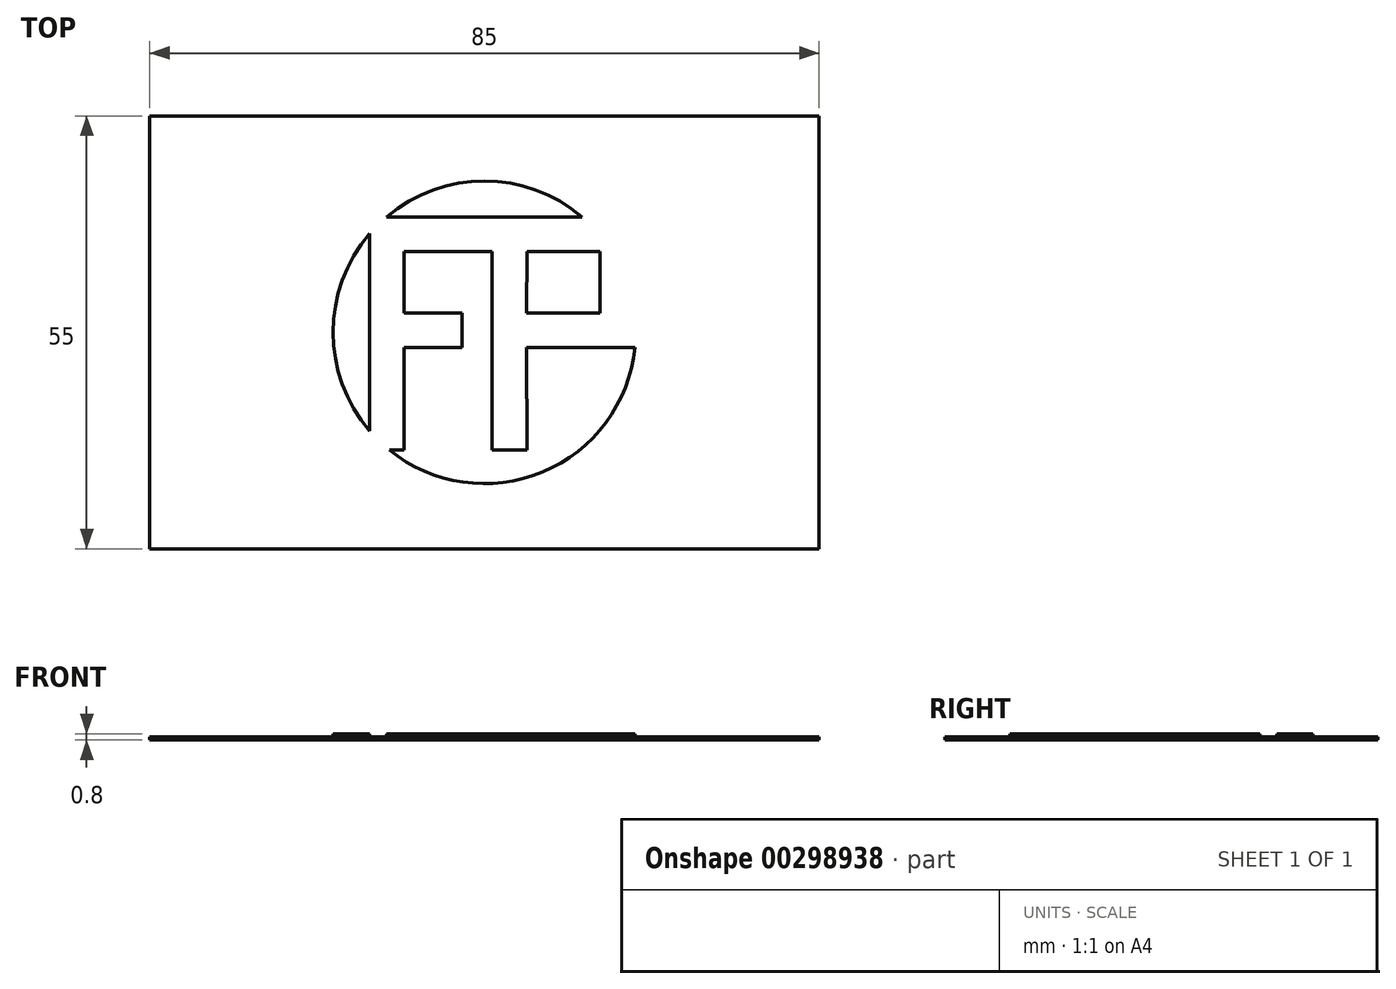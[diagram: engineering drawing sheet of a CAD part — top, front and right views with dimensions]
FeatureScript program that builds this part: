
annotation { "Feature Type Name" : "Feature", "Feature Type Description" : "" }
export const myFeature = defineFeature(function(context is Context, id is Id, definition is map)
    precondition{}
    {
        {
            var Q0;
            Q0=qCreatedBy(makeId("Top.planeOp"),FACE);
            var sketch = newSketch(context, id + "F0", { "sketchPlane" : qUnion([Q0])});
            skLineSegment(sketch, "E0.bottom", {"start": v(-42.5, 27.5) * mm, "end": v(42.5, 27.5) * mm});
            skLineSegment(sketch, "E0.top", {"start": v(-42.5, -27.5) * mm, "end": v(42.5, -27.5) * mm});
            skLineSegment(sketch, "E0.left", {"start": v(-42.5, 27.5) * mm, "end": v(-42.5, -27.5) * mm});
            skLineSegment(sketch, "E0.right", {"start": v(42.5, 27.5) * mm, "end": v(42.5, -27.5) * mm});
            skSolve(sketch);
        }
        {
            var Q0;
            Q0=makeQuery(id+"F0.imprint","IMPRINT",FACE,{"disambiguationData":[TD([[makeQuery(id+"F0.imprint","IMPRINT",EDGE,{"derivedFrom":sQuery(id+"F0.wireOp",EDGE,"E0.bottom")}),-1.0]])]});
            extrude(context, id + "F1", {"entities" : qUnion([Q0]), "depth" : 0.4 * mm});
        }
        {
            var Q0;
            Q0=makeQuery(id+"F1.opExtrude","CAP_FACE",FACE,{"disambiguationData":[OSD([sQuery(id+"F0.wireOp",EDGE,"E0.bottom"),sQuery(id+"F0.wireOp",EDGE,"E0.top"),sQuery(id+"F0.wireOp",EDGE,"E0.left"),sQuery(id+"F0.wireOp",EDGE,"E0.right")])],"isStart":false});
            var sketch = newSketch(context, id + "F2", { "sketchPlane" : qUnion([Q0])});
            skLineSegment(sketch, "E1", {"start": v(-10.17, 2.42) * mm, "end": v(-2.83, 2.42) * mm});
            skLineSegment(sketch, "E2", {"start": v(-2.83, 2.42) * mm, "end": v(-2.83, -1.95) * mm});
            skLineSegment(sketch, "E3", {"start": v(-2.83, -1.95) * mm, "end": v(-10.17, -1.95) * mm});
            skLineSegment(sketch, "E4", {"start": v(-10.17, -1.95) * mm, "end": v(-10.17, -14.95) * mm});
            skLineSegment(sketch, "E5", {"start": v(-10.17, -14.95) * mm, "end": v(-12.08, -14.95) * mm});
            skLineSegment(sketch, "E6", {"start": v(-14.59, -12.51) * mm, "end": v(-14.59, 12.51) * mm});
            skLineSegment(sketch, "E7", {"start": v(0.97, 10.26) * mm, "end": v(-10.17, 10.26) * mm});
            skLineSegment(sketch, "E8", {"start": v(-10.17, 10.26) * mm, "end": v(-10.17, 2.42) * mm});
            skLineSegment(sketch, "E9", {"start": v(19.21, -1.95) * mm, "end": v(5.38, -1.95) * mm});
            skLineSegment(sketch, "E10", {"start": v(5.38, -1.95) * mm, "end": v(5.38, -14.95) * mm});
            skLineSegment(sketch, "E11", {"start": v(5.38, -14.95) * mm, "end": v(0.97, -14.95) * mm});
            skLineSegment(sketch, "E12", {"start": v(0.97, -14.95) * mm, "end": v(0.97, 10.26) * mm});
            skLineSegment(sketch, "E13", {"start": v(14.71, 10.26) * mm, "end": v(5.38, 10.26) * mm});
            skLineSegment(sketch, "E14", {"start": v(5.38, 10.26) * mm, "end": v(5.38, 2.42) * mm});
            skLineSegment(sketch, "E15", {"start": v(5.38, 2.42) * mm, "end": v(14.71, 2.42) * mm});
            skLineSegment(sketch, "E16", {"start": v(14.71, 2.42) * mm, "end": v(14.71, 10.26) * mm});
            skLineSegment(sketch, "E17", {"start": v(-12.42, 14.67) * mm, "end": v(1.21, 14.67) * mm});
            skLineSegment(sketch, "E18", {"start": v(0.97, 14.67) * mm, "end": v(12.42, 14.67) * mm});
            skArc(sketch, "E19", {"start": v(12.42, 14.67) * mm, "mid": v(0, 19.22) * mm, "end": v(-12.42, 14.67) * mm});
            skArc(sketch, "E20.trimOffspring", {"start": v(-14.59, 12.51) * mm, "mid": v(-19.22, 0) * mm, "end": v(-14.59, -12.51) * mm});
            skArc(sketch, "E21.trimOffspring", {"start": v(-12.08, -14.95) * mm, "mid": v(7.39, -17.74) * mm, "end": v(19.12, -1.95) * mm});
            skSolve(sketch);
        }
        {
            var Q0;
            Q0 = qSketchRegion(id + "F2", true);
            extrude(context, id + "F3", {"entities" : qUnion([Q0]), "operationType" : NewBodyOperationType.ADD, "depth" : 0.4 * mm});
        }
    });
